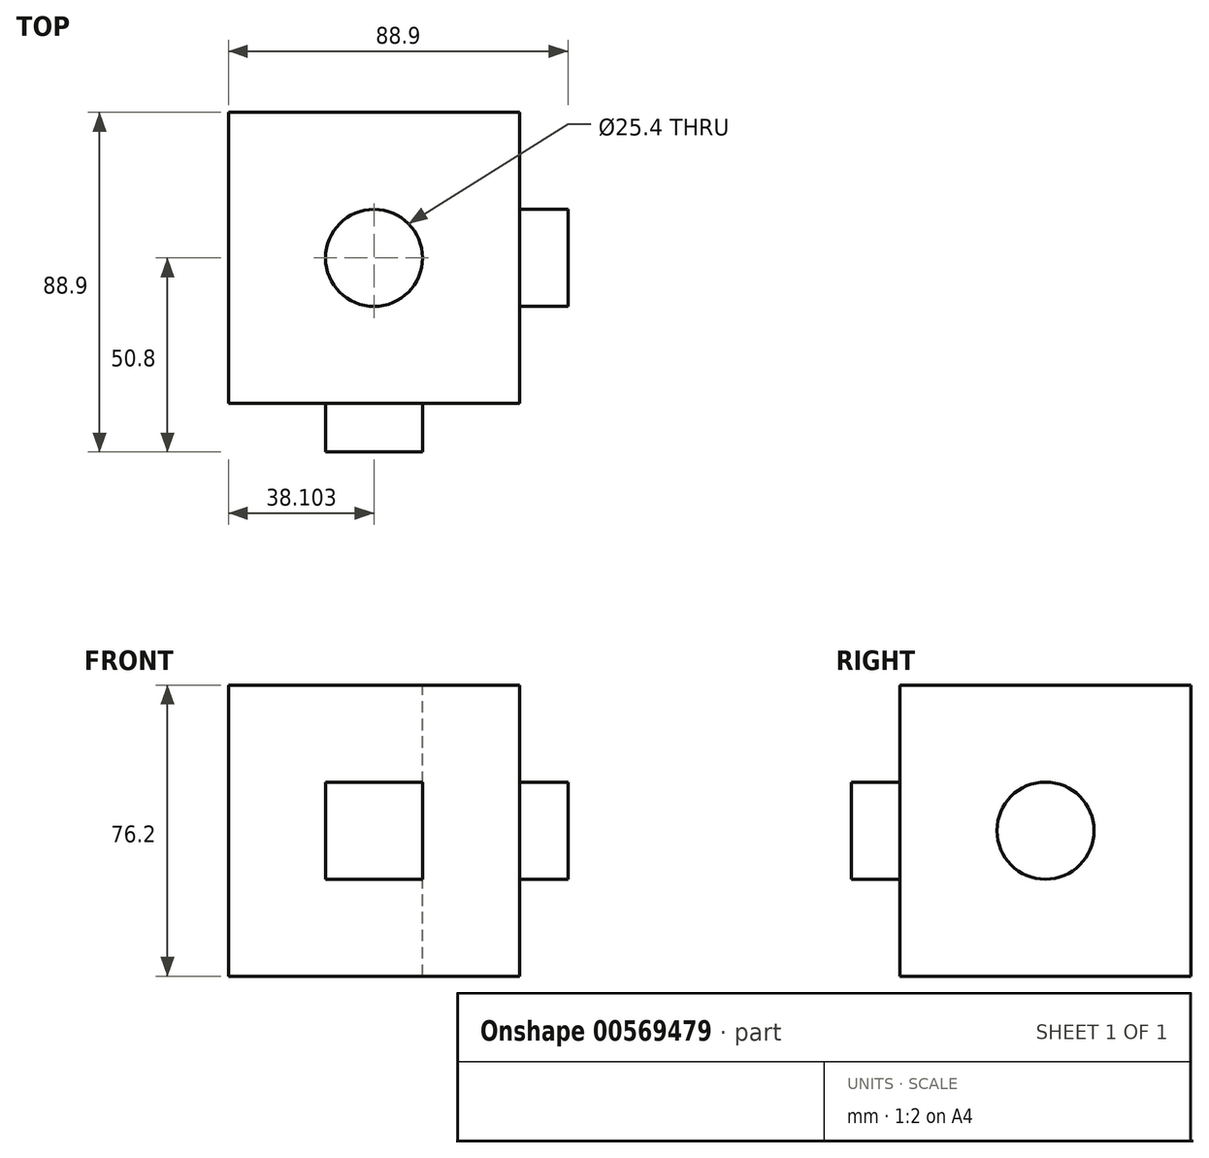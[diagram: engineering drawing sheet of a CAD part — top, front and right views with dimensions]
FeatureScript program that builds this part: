
annotation { "Feature Type Name" : "Feature", "Feature Type Description" : "" }
export const myFeature = defineFeature(function(context is Context, id is Id, definition is map)
    precondition{}
    {
        {
            var Q0;
            Q0=qCreatedBy(makeId("Front.planeOp"),FACE);
            var sketch = newSketch(context, id + "F0", { "sketchPlane" : qUnion([Q0])});
            skLineSegment(sketch, "E0.bottom", {"start": v(-50.14, 91.88) * mm, "end": v(26.06, 91.88) * mm});
            skLineSegment(sketch, "E0.top", {"start": v(-50.14, 15.68) * mm, "end": v(26.06, 15.68) * mm});
            skLineSegment(sketch, "E0.left", {"start": v(-50.14, 91.88) * mm, "end": v(-50.14, 15.68) * mm});
            skLineSegment(sketch, "E0.right", {"start": v(26.06, 91.88) * mm, "end": v(26.06, 15.68) * mm});
            skSolve(sketch);
        }
        {
            var Q0;
            Q0 = qSketchRegion(id + "F0", true);
            extrude(context, id + "F1", {"entities" : qUnion([Q0]), "depth" : 76.2 * mm, "offsetDistance" : 25.4 * mm});
        }
        {
            var Q0;
            Q0=makeQuery(id+"F1.opExtrude","CAP_FACE",FACE,{"disambiguationData":[OSD([sQuery(id+"F0.wireOp",EDGE,"E0.bottom"),sQuery(id+"F0.wireOp",EDGE,"E0.top"),sQuery(id+"F0.wireOp",EDGE,"E0.left"),sQuery(id+"F0.wireOp",EDGE,"E0.right")])],"isStart":false});
            var sketch = newSketch(context, id + "F2", { "sketchPlane" : qUnion([Q0])});
            skLineSegment(sketch, "E1.bottom", {"start": v(-24.74, 66.48) * mm, "end": v(0.66, 66.48) * mm});
            skLineSegment(sketch, "E1.top", {"start": v(-24.74, 41.08) * mm, "end": v(0.66, 41.08) * mm});
            skLineSegment(sketch, "E1.left", {"start": v(-24.74, 66.48) * mm, "end": v(-24.74, 41.08) * mm});
            skLineSegment(sketch, "E1.right", {"start": v(0.66, 66.48) * mm, "end": v(0.66, 41.08) * mm});
            skSolve(sketch);
        }
        {
            var Q0;
            Q0=makeQuery(id+"F2.imprint","IMPRINT",FACE,{"disambiguationData":[TD([[makeQuery(id+"F2.imprint","IMPRINT",EDGE,{"derivedFrom":sQuery(id+"F2.wireOp",EDGE,"E1.bottom")}),-1.0]])]});
            extrude(context, id + "F3", {"entities" : qUnion([Q0]), "operationType" : NewBodyOperationType.ADD, "depth" : 12.7 * mm, "offsetDistance" : 25.4 * mm});
        }
        {
            var Q0;
            Q0=makeQuery(id+"F1.opExtrude","SWEPT_FACE",FACE,{"disambiguationData":[OSD([sQuery(id+"F0.wireOp",EDGE,"E0.right")])]});
            var sketch = newSketch(context, id + "F4", { "sketchPlane" : qUnion([Q0])});
            skCircle(sketch, "E2", {"center": v(-38.1, 53.78) * mm, "radius": 12.7 * mm});
            skSolve(sketch);
        }
        {
            var Q0;
            Q0 = qSketchRegion(id + "F4", true);
            extrude(context, id + "F5", {"entities" : qUnion([Q0]), "operationType" : NewBodyOperationType.ADD, "depth" : 12.7 * mm, "offsetDistance" : 25.4 * mm});
        }
        {
            var Q0;
            Q0=makeQuery(id+"F1.opExtrude","SWEPT_FACE",FACE,{"disambiguationData":[OSD([sQuery(id+"F0.wireOp",EDGE,"E0.bottom")])]});
            var sketch = newSketch(context, id + "F6", { "sketchPlane" : qUnion([Q0])});
            skPoint(sketch, "E3", {"position": v(-12.04, -38.1) * mm});
            skPoint(sketch, "E3.positionSnap0", {"position": v(-12.04, -76.2) * mm});
            skPoint(sketch, "E3.positionSnap1", {"position": v(26.06, -38.1) * mm});
            skSolve(sketch);
        }
        {
            var Q0;
            Q0=sQuery(id+"F6.wireOp",VERTEX,"E3");
            var Q1;
            Q1=makeQuery(id+"F1.opExtrude","SWEPT_BODY",BODY,{"disambiguationData":[OSD([sQuery(id+"F0.wireOp",EDGE,"E0.bottom"),sQuery(id+"F0.wireOp",EDGE,"E0.top"),sQuery(id+"F0.wireOp",EDGE,"E0.left"),sQuery(id+"F0.wireOp",EDGE,"E0.right")])]});
            hole(context, id + "F7", {"style" : HoleStyle.SIMPLE, "endStyle" : HoleEndStyle.THROUGH, "holeDiameter" : 25.4 * mm, "isTappedThrough" : true, "tappedDepth" : 12.7 * mm, "tapClearance" : 3, "startFromSketch" : true, "locations" : qUnion([Q0]), "scope" : qUnion([Q1])});
        }
    });
